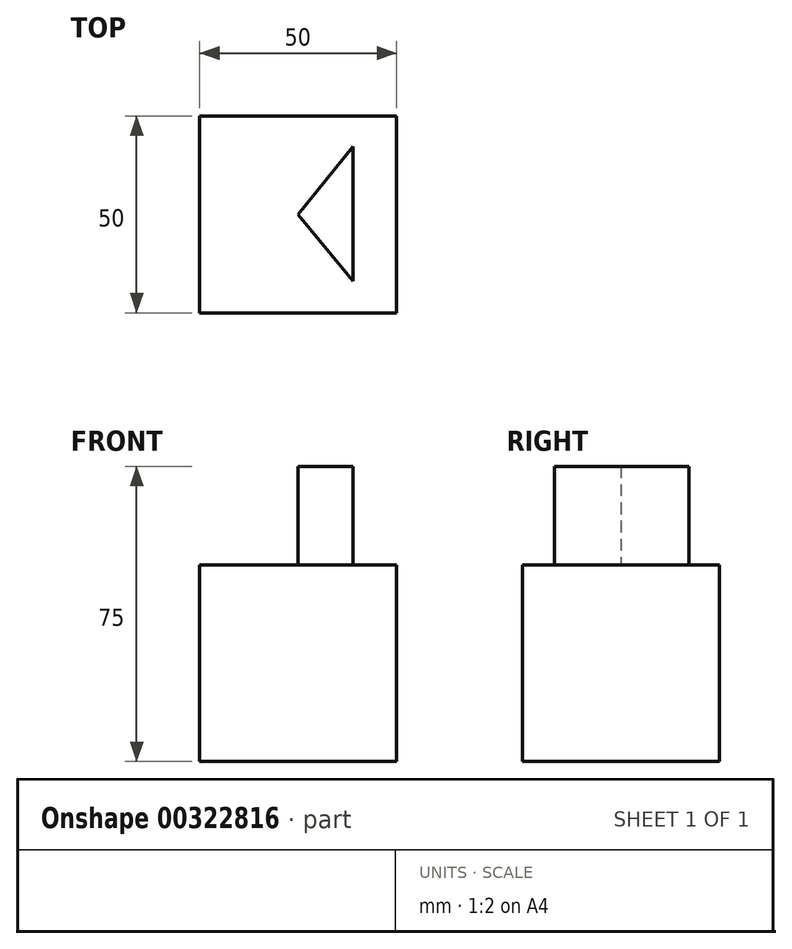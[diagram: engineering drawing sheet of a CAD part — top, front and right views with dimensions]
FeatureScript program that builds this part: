
annotation { "Feature Type Name" : "Feature", "Feature Type Description" : "" }
export const myFeature = defineFeature(function(context is Context, id is Id, definition is map)
    precondition{}
    {
        {
            var Q0;
            Q0=qCreatedBy(makeId("Top.planeOp"),FACE);
            var sketch = newSketch(context, id + "F0", { "sketchPlane" : qUnion([Q0])});
            skLineSegment(sketch, "E0", {"start": v(0, 44.87) * mm, "end": v(0, -30.94) * mm, "construction": true});
            skLineSegment(sketch, "E1", {"start": v(-41.87, 0) * mm, "end": v(40.07, 0) * mm, "construction": true});
            skLineSegment(sketch, "E2", {"start": v(-25, 25) * mm, "end": v(-25, -25) * mm});
            skLineSegment(sketch, "E3", {"start": v(-25, 25) * mm, "end": v(25, 25) * mm});
            skLineSegment(sketch, "E4.MirrorCS", {"start": v(-25, -25) * mm, "end": v(25, -25) * mm});
            skLineSegment(sketch, "E5.MirrorCS", {"start": v(25, 25) * mm, "end": v(25, -25) * mm});
            skPoint(sketch, "E6.orphan", {"position": v(25, 34) * mm});
            skPoint(sketch, "E7.orphan", {"position": v(32.12, 25) * mm});
            skPoint(sketch, "E8.orphan", {"position": v(32.12, -25) * mm});
            skPoint(sketch, "E9.orphan", {"position": v(25, -34.3) * mm});
            skPoint(sketch, "E10.orphan", {"position": v(-25, -34.3) * mm});
            skPoint(sketch, "E11.orphan", {"position": v(-37.07, -25) * mm});
            skPoint(sketch, "E12.orphan", {"position": v(-37.07, 25) * mm});
            skPoint(sketch, "E13.orphan", {"position": v(-25, 34) * mm});
            skSolve(sketch);
        }
        {
            var Q0;
            Q0 = qSketchRegion(id + "F0", true);
            extrude(context, id + "F1", {"entities" : qUnion([Q0]), "depth" : 50 * mm});
        }
        {
            var Q0;
            Q0=makeQuery(id+"F1.opExtrude","CAP_FACE",FACE,{"disambiguationData":[OSD([sQuery(id+"F0.wireOp",EDGE,"E2"),sQuery(id+"F0.wireOp",EDGE,"E3"),sQuery(id+"F0.wireOp",EDGE,"E4.MirrorCS"),sQuery(id+"F0.wireOp",EDGE,"E5.MirrorCS")])],"isStart":false});
            var sketch = newSketch(context, id + "F2", { "sketchPlane" : qUnion([Q0])});
            skLineSegment(sketch, "E14", {"start": v(0, 0) * mm, "end": v(13.97, 17.26) * mm});
            skLineSegment(sketch, "E15", {"start": v(13.97, 17.26) * mm, "end": v(13.97, -16.88) * mm});
            skLineSegment(sketch, "E16", {"start": v(0, 0) * mm, "end": v(13.97, -16.88) * mm});
            skSolve(sketch);
        }
        {
            var Q0;
            Q0=makeQuery(id+"F2.imprint","IMPRINT",FACE,{"disambiguationData":[TD([[makeQuery(id+"F2.imprint","IMPRINT",EDGE,{"derivedFrom":sQuery(id+"F2.wireOp",EDGE,"E14")}),-1.0]])]});
            extrude(context, id + "F3", {"entities" : qUnion([Q0]), "operationType" : NewBodyOperationType.ADD, "depth" : 25 * mm});
        }
    });
